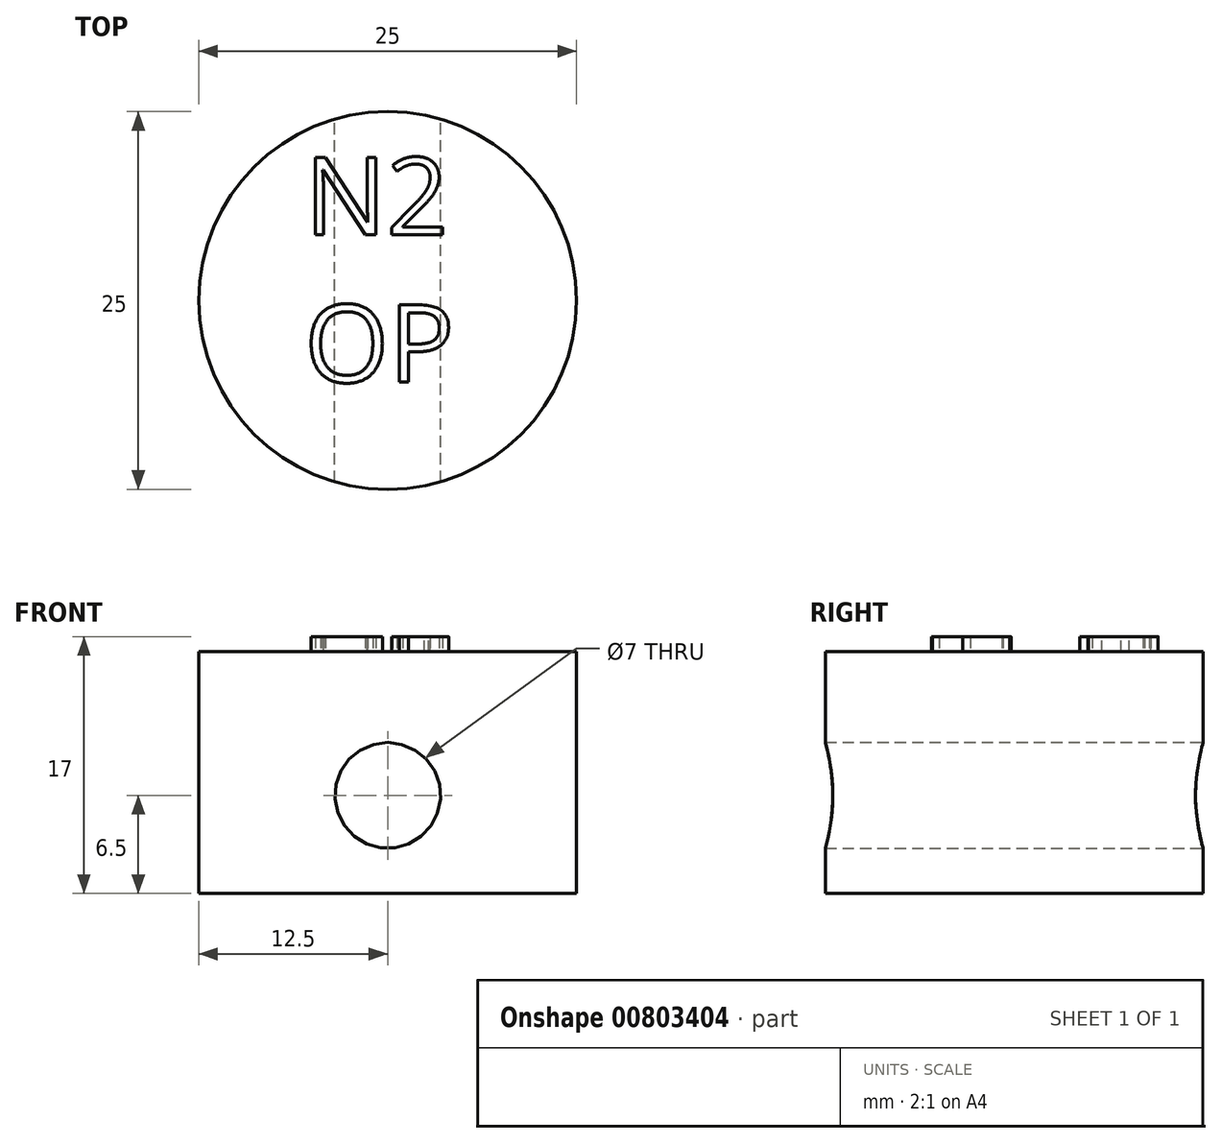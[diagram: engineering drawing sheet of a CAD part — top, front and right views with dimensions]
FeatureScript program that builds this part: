
annotation { "Feature Type Name" : "Feature", "Feature Type Description" : "" }
export const myFeature = defineFeature(function(context is Context, id is Id, definition is map)
    precondition{}
    {
        {
            var Q0;
            Q0=qCreatedBy(makeId("Top.planeOp"),FACE);
            var sketch = newSketch(context, id + "F0", { "sketchPlane" : qUnion([Q0])});
            skCircle(sketch, "E0", {"center": v(0, 0) * mm, "radius": 12.5 * mm});
            skSolve(sketch);
        }
        {
            var Q0;
            Q0=qSketchRegion(id+"F0",true);
            extrude(context, id + "F1", {"entities" : qUnion([Q0]), "depth" : 16 * mm, "offsetDistance" : 25 * mm});
        }
        {
            var Q0;
            Q0=qCreatedBy(makeId("Front.planeOp"),FACE);
            cPlane(context, id + "F2", {"entities" : qUnion([Q0]), "cplaneType" : CPlaneType.OFFSET, "offset" : 12.5 * mm, "oppositeDirection" : true, "width" : 150 * mm, "height" : 150 * mm});
        }
        {
            var Q0;
            Q0=qCreatedBy(id+"F2.planeOp",FACE);
            var sketch = newSketch(context, id + "F3", { "sketchPlane" : qUnion([Q0])});
            skLineSegment(sketch, "E1", {"start": v(0, 0) * mm, "end": v(0, 16) * mm, "construction": true});
            skPoint(sketch, "E2", {"position": v(0, 6.5) * mm});
            skCircle(sketch, "E3", {"center": v(0, 6.5) * mm, "radius": 3.5 * mm});
            skSolve(sketch);
        }
        {
            var Q0;
            Q0=makeQuery(id+"F3.imprint","IMPRINT",FACE,{"disambiguationData":[TD([[makeQuery(id+"F3.imprint","IMPRINT",EDGE,{"derivedFrom":sQuery(id+"F3.wireOp",EDGE,"E3")}),1.0]])]});
            extrude(context, id + "F4", {"entities" : qUnion([Q0]), "operationType" : NewBodyOperationType.REMOVE, "endBound" : BoundingType.THROUGH_ALL, "depth" : 25 * mm, "offsetDistance" : 25 * mm});
        }
        {
            var Q0;
            Q0=makeQuery(id+"F1.opExtrude","CAP_FACE",FACE,{"disambiguationData":[OSD([sQuery(id+"F0.wireOp",EDGE,"E0")])],"isStart":false});
            var sketch = newSketch(context, id + "F5", { "sketchPlane" : qUnion([Q0])});
            skText(sketch, "E4", { "text": "N2\nOP", "fontName": "OpenSans-Regular.ttf"});
            skPoint(sketch, "E5", {"position": v(0, 12.5) * mm});
            skPoint(sketch, "E6", {"position": v(-12.5, 0) * mm});
            const initialGuessF5  = {"E4": [-0.0055, 0.00434, 1, 0, 0.00516]};
            skSetInitialGuess(sketch, initialGuessF5);
            skSolve(sketch);
        }
        {
            var Q0;
            Q0=qSketchRegion(id+"F5",true);
            extrude(context, id + "F6", {"entities" : qUnion([Q0]), "operationType" : NewBodyOperationType.ADD, "depth" : 1 * mm, "offsetDistance" : 25 * mm});
        }
    });
